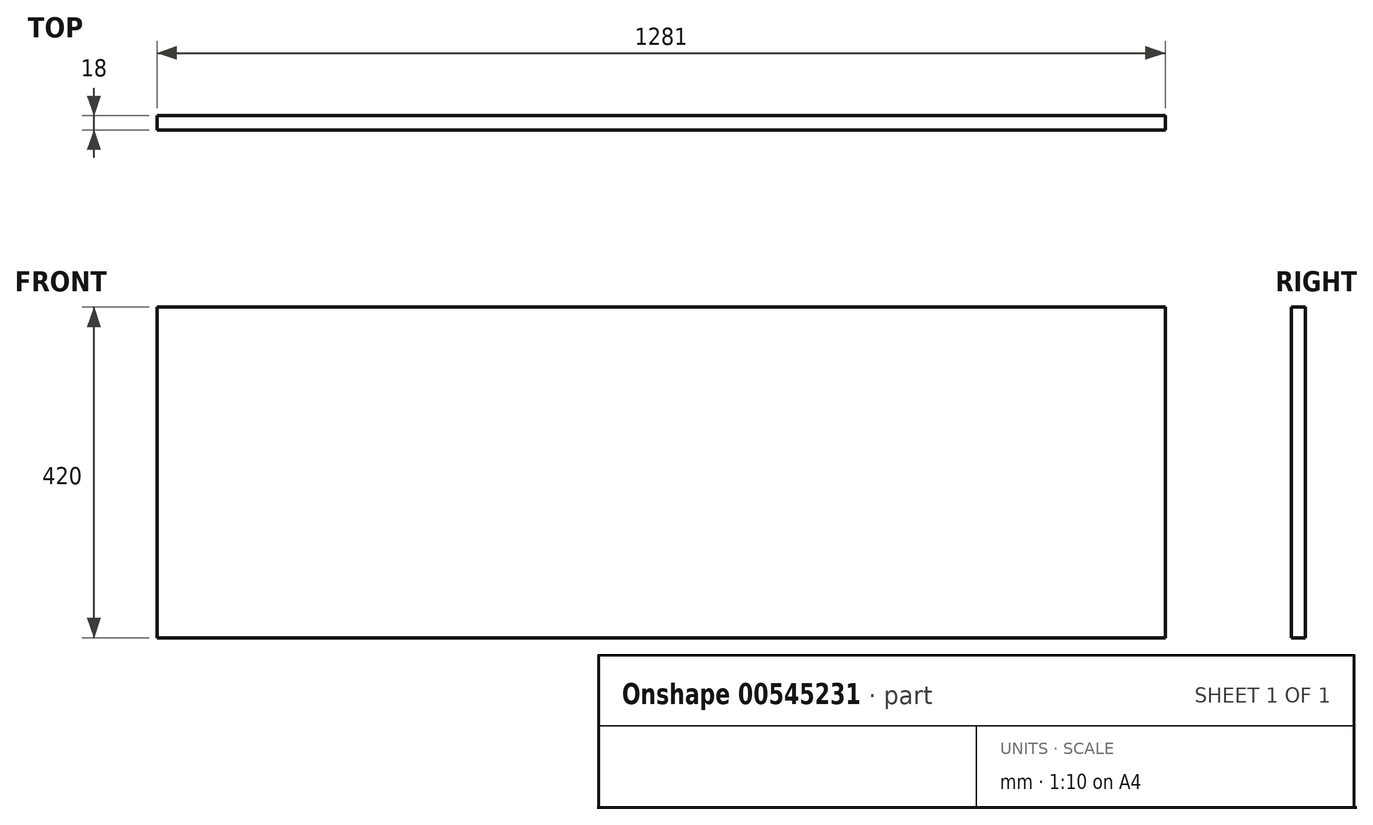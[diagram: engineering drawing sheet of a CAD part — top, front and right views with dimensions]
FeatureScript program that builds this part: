
annotation { "Feature Type Name" : "Feature", "Feature Type Description" : "" }
export const myFeature = defineFeature(function(context is Context, id is Id, definition is map)
    precondition{}
    {
        {
            var Q0;
            Q0=qCreatedBy(makeId("Front.planeOp"),FACE);
            var sketch = newSketch(context, id + "F0", { "sketchPlane" : qUnion([Q0])});
            skLineSegment(sketch, "E0.bottom", {"start": v(-619.65, -284.24) * mm, "end": v(661.35, -284.24) * mm});
            skLineSegment(sketch, "E0.top", {"start": v(-619.65, 135.76) * mm, "end": v(661.35, 135.76) * mm});
            skLineSegment(sketch, "E0.left", {"start": v(-619.65, -284.24) * mm, "end": v(-619.65, 135.76) * mm});
            skLineSegment(sketch, "E0.right", {"start": v(661.35, -284.24) * mm, "end": v(661.35, 135.76) * mm});
            skSolve(sketch);
        }
        {
            var Q0;
            Q0 = qSketchRegion(id + "F0", true);
            extrude(context, id + "F1", {"entities" : qUnion([Q0]), "depth" : 18 * mm, "offsetDistance" : 25 * mm});
        }
    });
